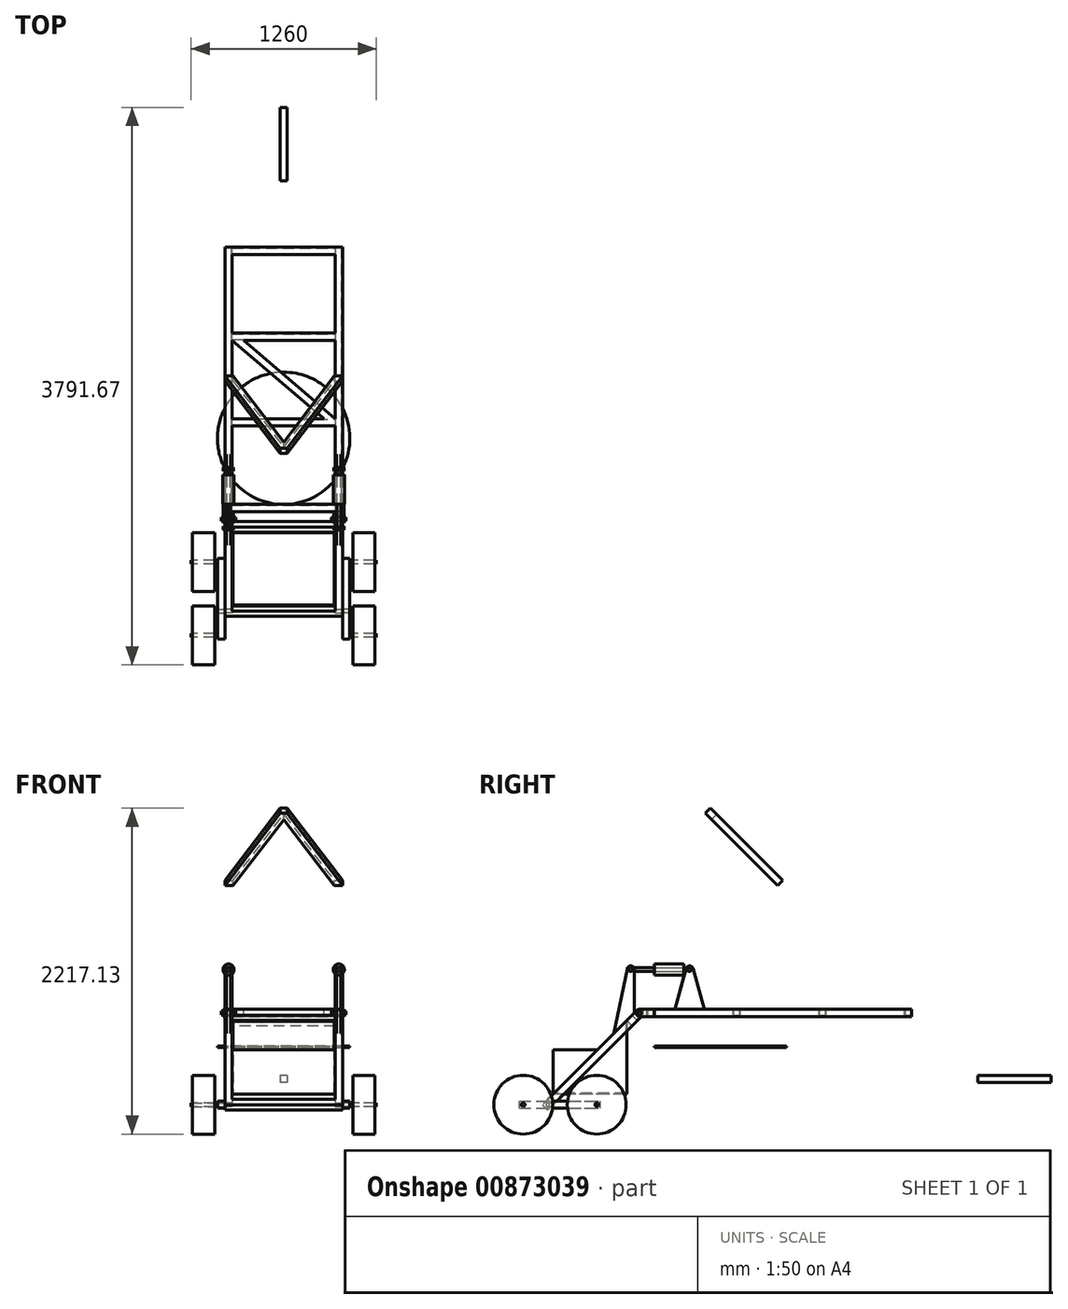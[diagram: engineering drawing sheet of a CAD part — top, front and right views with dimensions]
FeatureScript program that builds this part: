
annotation { "Feature Type Name" : "Feature", "Feature Type Description" : "" }
export const myFeature = defineFeature(function(context is Context, id is Id, definition is map)
    precondition{}
    {
        {
            assignVariable(context, id + "F0", {"name" : "TopLength", "anyValue" : 1800});
        }
        {
            assignVariable(context, id + "F1", {"name" : "PipeWidth", "anyValue" : 50});
        }
        {
            assignVariable(context, id + "F2", {"name" : "PipeThickness", "anyValue" : 5});
        }
        {
            var Q0;
            Q0=qCreatedBy(makeId("Front.planeOp"),FACE);
            var sketch = newSketch(context, id + "F3", { "sketchPlane" : qUnion([Q0])});
            skLineSegment(sketch, "E0.bottom", {"start": v(400, -25) * mm, "end": v(350, -25) * mm});
            skLineSegment(sketch, "E0.top", {"start": v(400, 25) * mm, "end": v(350, 25) * mm});
            skLineSegment(sketch, "E0.left", {"start": v(400, -25) * mm, "end": v(400, 25) * mm});
            skLineSegment(sketch, "E0.right", {"start": v(350, -25) * mm, "end": v(350, 25) * mm});
            skPoint(sketch, "E0.middle", {"position": v(375, 0) * mm});
            skSolve(sketch);
        }
        {
            var Q0;
            Q0=qSketchRegion(id+"F3",true);
            extrude(context, id + "F4", {"entities" : qUnion([Q0]), "endBound" : BoundingType.SYMMETRIC, "depth" : (getVariable(context, 'TopLength')) * mm, "offsetDistance" : 25 * mm});
        }
        {
            var Q0;
            Q0=makeQuery(id+"F4.opExtrude","CAP_FACE",FACE,{"disambiguationData":[OSD([sQuery(id+"F3.wireOp",EDGE,"E0.bottom"),sQuery(id+"F3.wireOp",EDGE,"E0.top"),sQuery(id+"F3.wireOp",EDGE,"E0.left"),sQuery(id+"F3.wireOp",EDGE,"E0.right")])],"isStart":false});
            var Q1;
            Q1=makeQuery(id+"F4.opExtrude","CAP_FACE",FACE,{"disambiguationData":[OSD([sQuery(id+"F3.wireOp",EDGE,"E0.bottom"),sQuery(id+"F3.wireOp",EDGE,"E0.top"),sQuery(id+"F3.wireOp",EDGE,"E0.left"),sQuery(id+"F3.wireOp",EDGE,"E0.right")])],"isStart":true});
            shell(context, id + "F5", {"entities" : qUnion([Q0, Q1]), "thickness" : (getVariable(context, 'PipeThickness')) * mm});
        }
        {
            var Q0;
            Q0=makeQuery(id+"F4.opExtrude","SWEPT_BODY",BODY,{"disambiguationData":[OSD([sQuery(id+"F3.wireOp",EDGE,"E0.bottom"),sQuery(id+"F3.wireOp",EDGE,"E0.top"),sQuery(id+"F3.wireOp",EDGE,"E0.left"),sQuery(id+"F3.wireOp",EDGE,"E0.right")])]});
            var Q1;
            Q1=qCreatedBy(makeId("Right.planeOp"),FACE);
            mirror(context, id + "F6", {"entities" : qUnion([Q0]), "mirrorPlane" : qUnion([Q1])});
        }
        {
            var Q0;
            Q0=makeQuery(id+"F4.opExtrude","SWEPT_FACE",FACE,{"disambiguationData":[OSD([sQuery(id+"F3.wireOp",EDGE,"E0.right")])]});
            var sketch = newSketch(context, id + "F7", { "sketchPlane" : qUnion([Q0])});
            skLineSegment(sketch, "E1.bottom", {"start": v(900, 25) * mm, "end": v(850, 25) * mm});
            skLineSegment(sketch, "E1.top", {"start": v(900, -25) * mm, "end": v(850, -25) * mm});
            skLineSegment(sketch, "E1.left", {"start": v(900, 25) * mm, "end": v(900, -25) * mm});
            skLineSegment(sketch, "E1.right", {"start": v(850, 25) * mm, "end": v(850, -25) * mm});
            skLineSegment(sketch, "E2.bottom", {"start": v(855, 20) * mm, "end": v(895, 20) * mm});
            skLineSegment(sketch, "E2.top", {"start": v(855, -20) * mm, "end": v(895, -20) * mm});
            skLineSegment(sketch, "E2.left", {"start": v(855, 20) * mm, "end": v(855, -20) * mm});
            skLineSegment(sketch, "E2.right", {"start": v(895, 20) * mm, "end": v(895, -20) * mm});
            skLineSegment(sketch, "E3.1.0.0", {"start": v(271.67, -20) * mm, "end": v(311.67, -20) * mm});
            skLineSegment(sketch, "E3.1.0.1", {"start": v(311.67, 20) * mm, "end": v(311.67, -20) * mm});
            skLineSegment(sketch, "E3.1.0.2", {"start": v(316.67, 25) * mm, "end": v(266.67, 25) * mm});
            skLineSegment(sketch, "E3.1.0.3", {"start": v(316.67, 25) * mm, "end": v(316.67, -25) * mm});
            skLineSegment(sketch, "E3.1.0.4", {"start": v(271.67, 20) * mm, "end": v(311.67, 20) * mm});
            skLineSegment(sketch, "E3.1.0.5", {"start": v(316.67, -25) * mm, "end": v(266.67, -25) * mm});
            skLineSegment(sketch, "E3.1.0.6", {"start": v(271.67, 20) * mm, "end": v(271.67, -20) * mm});
            skLineSegment(sketch, "E3.1.0.7", {"start": v(266.67, 25) * mm, "end": v(266.67, -25) * mm});
            skLineSegment(sketch, "E3.2.0.0", {"start": v(-311.67, -20) * mm, "end": v(-271.67, -20) * mm});
            skLineSegment(sketch, "E3.2.0.1", {"start": v(-271.67, 20) * mm, "end": v(-271.67, -20) * mm});
            skLineSegment(sketch, "E3.2.0.2", {"start": v(-266.67, 25) * mm, "end": v(-316.67, 25) * mm});
            skLineSegment(sketch, "E3.2.0.3", {"start": v(-266.67, 25) * mm, "end": v(-266.67, -25) * mm});
            skLineSegment(sketch, "E3.2.0.4", {"start": v(-311.67, 20) * mm, "end": v(-271.67, 20) * mm});
            skLineSegment(sketch, "E3.2.0.5", {"start": v(-266.67, -25) * mm, "end": v(-316.67, -25) * mm});
            skLineSegment(sketch, "E3.2.0.6", {"start": v(-311.67, 20) * mm, "end": v(-311.67, -20) * mm});
            skLineSegment(sketch, "E3.2.0.7", {"start": v(-316.67, 25) * mm, "end": v(-316.67, -25) * mm});
            skLineSegment(sketch, "E3.3.0.0", {"start": v(-895, -20) * mm, "end": v(-855, -20) * mm});
            skLineSegment(sketch, "E3.3.0.1", {"start": v(-855, 20) * mm, "end": v(-855, -20) * mm});
            skLineSegment(sketch, "E3.3.0.2", {"start": v(-850, 25) * mm, "end": v(-900, 25) * mm});
            skLineSegment(sketch, "E3.3.0.3", {"start": v(-850, 25) * mm, "end": v(-850, -25) * mm});
            skLineSegment(sketch, "E3.3.0.4", {"start": v(-895, 20) * mm, "end": v(-855, 20) * mm});
            skLineSegment(sketch, "E3.3.0.5", {"start": v(-850, -25) * mm, "end": v(-900, -25) * mm});
            skLineSegment(sketch, "E3.3.0.6", {"start": v(-895, 20) * mm, "end": v(-895, -20) * mm});
            skLineSegment(sketch, "E3.3.0.7", {"start": v(-900, 25) * mm, "end": v(-900, -25) * mm});
            skLineSegment(sketch, "E3.direction1", {"start": v(850, -25) * mm, "end": v(266.67, -25) * mm, "construction": true});
            skSolve(sketch);
        }
        {
            var Q0;
            Q0=qSketchRegion(id+"F7",true);
            extrude(context, id + "F8", {"entities" : qUnion([Q0]), "operationType" : NewBodyOperationType.ADD, "endBound" : BoundingType.UP_TO_NEXT, "depth" : 25 * mm, "offsetDistance" : 25 * mm});
        }
        {
            assignVariable(context, id + "F9", {"name" : "TopHeight", "anyValue" : 800});
        }
        {
            var Q0;
            {var subQ0=makeQuery(id+"F4.opExtrude","SWEPT_FACE",FACE,{"disambiguationData":[OSD([sQuery(id+"F3.wireOp",EDGE,"E0.bottom")])]});Q0=makeQuery(id+"F8.boolean.opBoolean","MERGE",FACE,{"derivedFrom":[subQ0,makeQuery(id+"F6.opPattern","COPY",FACE,{"derivedFrom":subQ0,"instanceName":"1"}),makeQuery(id+"F8.opExtrude","SWEPT_FACE",FACE,{"disambiguationData":[OSD([sQuery(id+"F7.wireOp",EDGE,"E1.top")])]}),makeQuery(id+"F8.opExtrude","SWEPT_FACE",FACE,{"disambiguationData":[OSD([sQuery(id+"F7.wireOp",EDGE,"E3.1.0.5")])]}),makeQuery(id+"F8.opExtrude","SWEPT_FACE",FACE,{"disambiguationData":[OSD([sQuery(id+"F7.wireOp",EDGE,"E3.2.0.5")])]}),makeQuery(id+"F8.opExtrude","SWEPT_FACE",FACE,{"disambiguationData":[OSD([sQuery(id+"F7.wireOp",EDGE,"E3.3.0.5")])]})]});}
            cPlane(context, id + "F10", {"entities" : qUnion([Q0]), "cplaneType" : CPlaneType.OFFSET, "offset" : (getVariable(context, 'TopHeight')) * mm, "width" : 150 * mm, "height" : 150 * mm});
        }
        {
            var Q0;
            Q0=makeQuery(id+"F6.opPattern","COPY",FACE,{"derivedFrom":makeQuery(id+"F4.opExtrude","SWEPT_FACE",FACE,{"disambiguationData":[OSD([sQuery(id+"F3.wireOp",EDGE,"E0.left")])]}),"instanceName":"1"});
            var sketch = newSketch(context, id + "F11", { "sketchPlane" : qUnion([Q0])});
            skLineSegment(sketch, "E4", {"start": v(967.68, 17.68) * mm, "end": v(1610.36, -625) * mm});
            skLineSegment(sketch, "E5", {"start": v(1610.36, -625) * mm, "end": v(1575, -660.36) * mm});
            skLineSegment(sketch, "E6", {"start": v(1575, -660.36) * mm, "end": v(932.32, -17.68) * mm});
            skCircle(sketch, "E7", {"center": v(1092.75, -625) * mm, "radius": 200 * mm, "construction": true});
            skCircle(sketch, "E8", {"center": v(1592.75, -625) * mm, "radius": 200 * mm, "construction": true});
            skCircle(sketch, "E9", {"center": v(1575, -625) * mm, "radius": 12.5 * mm});
            skLineSegment(sketch, "E10", {"start": v(1575, -625) * mm, "end": v(1615.74, -665.74) * mm, "construction": true});
            skCircle(sketch, "E11", {"center": v(950, 0) * mm, "radius": 12.5 * mm});
            skPoint(sketch, "E11.centerSnap0", {"position": v(900, 0) * mm});
            skLineSegment(sketch, "E12", {"start": v(950, 0) * mm, "end": v(1014.37, -64.37) * mm, "construction": true});
            skArc(sketch, "E13", {"start": v(967.68, 17.68) * mm, "mid": v(932.32, 17.68) * mm, "end": v(932.32, -17.68) * mm});
            skSolve(sketch);
        }
        {
            var Q0;
            Q0=qSketchRegion(id+"F11",true);
            extrude(context, id + "F12", {"entities" : qUnion([Q0]), "oppositeDirection" : true, "depth" : (getVariable(context, 'PipeWidth')) * mm, "offsetDistance" : 25 * mm});
        }
        {
            var Q0;
            Q0=makeQuery(id+"F12.opExtrude","SWEPT_BODY",BODY,{"disambiguationData":[OSD([sQuery(id+"F11.wireOp",EDGE,"E4"),sQuery(id+"F11.wireOp",EDGE,"E5"),sQuery(id+"F11.wireOp",EDGE,"E6"),sQuery(id+"F11.wireOp",EDGE,"p147dLJD-aIzN-PVzP-jr04-d3EFBxcOCl1r"),sQuery(id+"F11.wireOp",EDGE,"E9")])]});
            var Q1;
            Q1=qCreatedBy(makeId("Right.planeOp"),FACE);
            mirror(context, id + "F13", {"operationType" : NewBodyOperationType.ADD, "entities" : qUnion([Q0]), "mirrorPlane" : qUnion([Q1])});
        }
        {
            var Q0;
            Q0=makeQuery(id+"F12.opExtrude","CAP_FACE",FACE,{"disambiguationData":[OSD([sQuery(id+"F11.wireOp",EDGE,"E4"),sQuery(id+"F11.wireOp",EDGE,"E5"),sQuery(id+"F11.wireOp",EDGE,"E6"),sQuery(id+"F11.wireOp",EDGE,"E9"),sQuery(id+"F11.wireOp",EDGE,"E11"),sQuery(id+"F11.wireOp",EDGE,"E13")])],"isStart":false});
            var sketch = newSketch(context, id + "F14", { "sketchPlane" : qUnion([Q0])});
            skLineSegment(sketch, "E14", {"start": v(-1575, -660.36) * mm, "end": v(-1539.64, -625) * mm});
            skLineSegment(sketch, "E15", {"start": v(-1575, -589.64) * mm, "end": v(-1539.64, -625) * mm});
            skLineSegment(sketch, "E16", {"start": v(-1575, -589.64) * mm, "end": v(-1610.36, -625) * mm});
            skLineSegment(sketch, "E17", {"start": v(-1575, -660.36) * mm, "end": v(-1610.36, -625) * mm});
            skSolve(sketch);
        }
        {
            var Q0;
            Q0=qSketchRegion(id+"F14",true);
            var Q1;
            Q1=makeQuery(id+"F13.opPattern","COPY",FACE,{"derivedFrom":makeQuery(id+"F12.opExtrude","CAP_FACE",FACE,{"disambiguationData":[OSD([sQuery(id+"F11.wireOp",EDGE,"E4"),sQuery(id+"F11.wireOp",EDGE,"E5"),sQuery(id+"F11.wireOp",EDGE,"E6"),sQuery(id+"F11.wireOp",EDGE,"E9"),sQuery(id+"F11.wireOp",EDGE,"E11"),sQuery(id+"F11.wireOp",EDGE,"E13")])],"isStart":false}),"instanceName":"1"});
            extrude(context, id + "F15", {"entities" : qUnion([Q0]), "operationType" : NewBodyOperationType.ADD, "endBound" : BoundingType.UP_TO_SURFACE, "depth" : (50 + 15) * mm, "endBoundEntityFace" : qUnion([Q1]), "offsetDistance" : 25 * mm});
        }
        {
            var Q0;
            Q0=makeQuery(id+"F13.boolean.opBoolean","MERGE",FACE,{"derivedFrom":[makeQuery(id+"F6.opPattern","COPY",FACE,{"derivedFrom":makeQuery(id+"F4.opExtrude","SWEPT_FACE",FACE,{"disambiguationData":[OSD([sQuery(id+"F3.wireOp",EDGE,"E0.left")])]}),"instanceName":"1"}),makeQuery(id+"F12.opExtrude","CAP_FACE",FACE,{"disambiguationData":[OSD([sQuery(id+"F11.wireOp",EDGE,"E4"),sQuery(id+"F11.wireOp",EDGE,"E5"),sQuery(id+"F11.wireOp",EDGE,"E6"),sQuery(id+"F11.wireOp",EDGE,"p147dLJD-aIzN-PVzP-jr04-d3EFBxcOCl1r"),sQuery(id+"F11.wireOp",EDGE,"E9")])],"isStart":true})]});
            var sketch = newSketch(context, id + "F16", { "sketchPlane" : qUnion([Q0])});
            skCircle(sketch, "E18.0.0", {"center": v(1575, -625) * mm, "radius": 12.5 * mm});
            skLineSegment(sketch, "E19.bottom", {"start": v(1766.67, -650) * mm, "end": v(1216.67, -650) * mm});
            skLineSegment(sketch, "E19.top", {"start": v(1766.67, -600) * mm, "end": v(1216.67, -600) * mm});
            skLineSegment(sketch, "E19.left", {"start": v(1766.67, -650) * mm, "end": v(1766.67, -600) * mm});
            skLineSegment(sketch, "E19.right", {"start": v(1216.67, -650) * mm, "end": v(1216.67, -600) * mm});
            skPoint(sketch, "E19.middle", {"position": v(1491.67, -625) * mm});
            skCircle(sketch, "E20", {"center": v(1741.67, -625) * mm, "radius": 12.5 * mm});
            skCircle(sketch, "E21", {"center": v(1241.67, -625) * mm, "radius": 12.5 * mm});
            skSolve(sketch);
        }
        {
            var Q0;
            Q0=qSketchRegion(id+"F16",true);
            extrude(context, id + "F17", {"entities" : qUnion([Q0]), "depth" : (getVariable(context, 'PipeWidth')) * mm, "offsetDistance" : 25 * mm});
        }
        {
            var Q0;
            Q0=makeQuery(id+"F17.opExtrude","CAP_FACE",FACE,{"disambiguationData":[OSD([sQuery(id+"F16.wireOp",EDGE,"E18.0.0"),sQuery(id+"F16.wireOp",EDGE,"E19.bottom"),sQuery(id+"F16.wireOp",EDGE,"E19.top"),sQuery(id+"F16.wireOp",EDGE,"E19.left"),sQuery(id+"F16.wireOp",EDGE,"E19.right"),sQuery(id+"F16.wireOp",EDGE,"E20"),sQuery(id+"F16.wireOp",EDGE,"E21")])],"isStart":false});
            var sketch = newSketch(context, id + "F18", { "sketchPlane" : qUnion([Q0])});
            skCircle(sketch, "E22.0", {"center": v(1741.67, -625) * mm, "radius": 12.5 * mm});
            skCircle(sketch, "E23.0", {"center": v(1241.67, -625) * mm, "radius": 12.5 * mm});
            skSolve(sketch);
        }
        {
            var Q0;
            Q0=qSketchRegion(id+"F18",true);
            var Q1;
            Q1=makeQuery(id+"F17.opExtrude","CAP_FACE",FACE,{"disambiguationData":[OSD([sQuery(id+"F16.wireOp",EDGE,"E18.0.0"),sQuery(id+"F16.wireOp",EDGE,"E19.bottom"),sQuery(id+"F16.wireOp",EDGE,"E19.top"),sQuery(id+"F16.wireOp",EDGE,"E19.left"),sQuery(id+"F16.wireOp",EDGE,"E19.right"),sQuery(id+"F16.wireOp",EDGE,"E20"),sQuery(id+"F16.wireOp",EDGE,"E21")])],"isStart":true});
            extrude(context, id + "F19", {"entities" : qUnion([Q0]), "operationType" : NewBodyOperationType.ADD, "depth" : (20 + 150 + 10) * mm, "offsetDistance" : 25 * mm, "hasSecondDirection" : true, "secondDirectionBound" : SecondDirectionBoundingType.UP_TO_SURFACE, "secondDirectionOppositeDirection" : true, "secondDirectionDepth" : 25 * mm, "secondDirectionBoundEntityFace" : qUnion([Q1])});
        }
        {
            var Q0;
            Q0=makeQuery(id+"F19.opExtrude","CAP_FACE",FACE,{"disambiguationData":[OSD([sQuery(id+"F18.wireOp",EDGE,"E23.0")])],"isStart":false});
            cPlane(context, id + "F20", {"entities" : qUnion([Q0]), "cplaneType" : CPlaneType.OFFSET, "offset" : 10 * mm, "oppositeDirection" : true, "width" : 150 * mm, "height" : 150 * mm});
        }
        {
            var Q0;
            Q0=qCreatedBy(id+"F20.planeOp",FACE);
            var sketch = newSketch(context, id + "F21", { "sketchPlane" : qUnion([Q0])});
            skCircle(sketch, "E24.0", {"center": v(1241.67, -625) * mm, "radius": 12.5 * mm});
            skCircle(sketch, "E25.0.0", {"center": v(1741.67, -625) * mm, "radius": 12.5 * mm});
            skCircle(sketch, "E26", {"center": v(1241.67, -625) * mm, "radius": 200 * mm});
            skCircle(sketch, "E27", {"center": v(1741.67, -625) * mm, "radius": 200 * mm});
            skSolve(sketch);
        }
        {
            var Q0;
            Q0=qSketchRegion(id+"F21",true);
            extrude(context, id + "F22", {"entities" : qUnion([Q0]), "oppositeDirection" : true, "depth" : 150 * mm, "offsetDistance" : 25 * mm});
        }
        {
            var Q0;
            Q0=makeQuery(id+"F22.opExtrude","SWEPT_BODY",BODY,{"disambiguationData":[OSD([sQuery(id+"F21.wireOp",EDGE,"E24.0"),sQuery(id+"F21.wireOp",EDGE,"E26")])]});
            var Q1;
            Q1=makeQuery(id+"F22.opExtrude","SWEPT_BODY",BODY,{"disambiguationData":[OSD([sQuery(id+"F21.wireOp",EDGE,"E25.0.0"),sQuery(id+"F21.wireOp",EDGE,"E27")])]});
            var Q2;
            Q2=makeQuery(id+"F17.opExtrude","SWEPT_BODY",BODY,{"disambiguationData":[OSD([sQuery(id+"F16.wireOp",EDGE,"E18.0.0"),sQuery(id+"F16.wireOp",EDGE,"E19.bottom"),sQuery(id+"F16.wireOp",EDGE,"E19.top"),sQuery(id+"F16.wireOp",EDGE,"E19.left"),sQuery(id+"F16.wireOp",EDGE,"E19.right"),sQuery(id+"F16.wireOp",EDGE,"E20"),sQuery(id+"F16.wireOp",EDGE,"E21")])]});
            var Q3;
            Q3=qCreatedBy(makeId("Right.planeOp"),FACE);
            mirror(context, id + "F23", {"entities" : qUnion([Q0, Q1, Q2]), "mirrorPlane" : qUnion([Q3])});
        }
        {
            var Q0;
            Q0=qCreatedBy(makeId("Right.planeOp"),FACE);
            var sketch = newSketch(context, id + "F24", { "sketchPlane" : qUnion([Q0])});
            skLineSegment(sketch, "E28.bottom", {"start": v(1850, -425) * mm, "end": v(1350, -425) * mm});
            skLineSegment(sketch, "E28.top", {"start": v(1850, -475) * mm, "end": v(1350, -475) * mm});
            skLineSegment(sketch, "E28.left", {"start": v(1850, -425) * mm, "end": v(1850, -475) * mm});
            skLineSegment(sketch, "E28.right", {"start": v(1350, -425) * mm, "end": v(1350, -475) * mm});
            skLineSegment(sketch, "E29", {"start": v(1350, -425) * mm, "end": v(900, 25) * mm, "construction": true});
            skSolve(sketch);
        }
        {
            var Q0;
            Q0=qSketchRegion(id+"F24",true);
            extrude(context, id + "F25", {"entities" : qUnion([Q0]), "endBound" : BoundingType.SYMMETRIC, "depth" : (getVariable(context, 'PipeWidth')) * mm, "offsetDistance" : 25 * mm});
        }
        {
            var Q0;
            Q0=makeQuery(id+"F4.opExtrude","CAP_VERTEX",VERTEX,{"disambiguationData":[OSD([sQuery(id+"F3.wireOp",EDGE,"E0.top"),sQuery(id+"F3.wireOp",EDGE,"E0.left")])],"isStart":true});
            var Q1;
            Q1=makeQuery(id+"F6.opPattern","COPY",VERTEX,{"derivedFrom":makeQuery(id+"F4.opExtrude","CAP_VERTEX",VERTEX,{"disambiguationData":[OSD([sQuery(id+"F3.wireOp",EDGE,"E0.top"),sQuery(id+"F3.wireOp",EDGE,"E0.left")])],"isStart":true}),"instanceName":"1"});
            var Q2;
            Q2=makeQuery(id+"F25.opExtrude","CAP_VERTEX",VERTEX,{"disambiguationData":[OSD([sQuery(id+"F24.wireOp",EDGE,"E28.bottom"),sQuery(id+"F24.wireOp",EDGE,"E28.right")])],"isStart":true});
            cPlane(context, id + "F26", {"entities" : qUnion([Q0, Q1, Q2]), "cplaneType" : CPlaneType.THREE_POINT, "offset" : 25 * mm, "width" : 150 * mm, "height" : 150 * mm});
        }
        {
            var Q0;
            Q0=qCreatedBy(id+"F26.planeOp",FACE);
            var sketch = newSketch(context, id + "F27", { "sketchPlane" : qUnion([Q0])});
            skLineSegment(sketch, "E30", {"start": v(400, 618.72) * mm, "end": v(25, 1314.7) * mm});
            skLineSegment(sketch, "E31", {"start": v(25, 1314.7) * mm, "end": v(-25, 1314.7) * mm});
            skLineSegment(sketch, "E32", {"start": v(-25, 1314.7) * mm, "end": v(-400, 618.72) * mm});
            skLineSegment(sketch, "E33", {"start": v(400, 618.72) * mm, "end": v(343.2, 618.72) * mm});
            skLineSegment(sketch, "E34", {"start": v(343.2, 618.72) * mm, "end": v(0, 1255.7) * mm});
            skLineSegment(sketch, "E35", {"start": v(0, 1255.7) * mm, "end": v(-343.2, 618.72) * mm});
            skLineSegment(sketch, "E36", {"start": v(-343.2, 618.72) * mm, "end": v(-400, 618.72) * mm});
            skSolve(sketch);
        }
        {
            var Q0;
            Q0=qSketchRegion(id+"F27",true);
            extrude(context, id + "F28", {"entities" : qUnion([Q0]), "operationType" : NewBodyOperationType.ADD, "oppositeDirection" : true, "depth" : 50 * mm, "offsetDistance" : 25 * mm});
        }
        {
            var Q0;
            Q0=makeQuery(id+"F6.opPattern","COPY",FACE,{"derivedFrom":makeQuery(id+"F4.opExtrude","SWEPT_FACE",FACE,{"disambiguationData":[OSD([sQuery(id+"F3.wireOp",EDGE,"E0.left")])]}),"instanceName":"1"});
            var sketch = newSketch(context, id + "F29", { "sketchPlane" : qUnion([Q0])});
            skLineSegment(sketch, "E37", {"start": v(850, 25) * mm, "end": v(850, -25) * mm});
            skLineSegment(sketch, "E38", {"start": v(850, -25) * mm, "end": v(950, -25) * mm});
            skLineSegment(sketch, "E39", {"start": v(850, 25) * mm, "end": v(950, 25) * mm});
            skCircle(sketch, "E40.0", {"center": v(950, 0) * mm, "radius": 12.5 * mm});
            skArc(sketch, "E41", {"start": v(950, 25) * mm, "mid": v(975, 0) * mm, "end": v(950, -25) * mm});
            skSolve(sketch);
        }
        {
            var Q0;
            Q0 = qSketchRegion(id + "F29", true);
            extrude(context, id + "F30", {"entities" : qUnion([Q0]), "depth" : 10 * mm, "offsetDistance" : 25 * mm});
        }
        {
            var Q0;
            Q0=makeQuery(id+"F12.opExtrude","CAP_FACE",FACE,{"disambiguationData":[OSD([sQuery(id+"F11.wireOp",EDGE,"E4"),sQuery(id+"F11.wireOp",EDGE,"E5"),sQuery(id+"F11.wireOp",EDGE,"E6"),sQuery(id+"F11.wireOp",EDGE,"E9"),sQuery(id+"F11.wireOp",EDGE,"E11"),sQuery(id+"F11.wireOp",EDGE,"E13")])],"isStart":false});
            var sketch = newSketch(context, id + "F31", { "sketchPlane" : qUnion([Q0])});
            skCircle(sketch, "E42.0", {"center": v(-950, 0) * mm, "radius": 12.5 * mm});
            skLineSegment(sketch, "E43", {"start": v(-950, -25) * mm, "end": v(-900, -25) * mm});
            skLineSegment(sketch, "E44", {"start": v(-900, -25) * mm, "end": v(-900, 25) * mm});
            skLineSegment(sketch, "E45", {"start": v(-900, 25) * mm, "end": v(-950, 25) * mm});
            skArc(sketch, "E46", {"start": v(-950, 25) * mm, "mid": v(-975, 0) * mm, "end": v(-950, -25) * mm});
            skSolve(sketch);
        }
        {
            var Q0;
            Q0 = qSketchRegion(id + "F31", true);
            extrude(context, id + "F32", {"entities" : qUnion([Q0]), "depth" : 10 * mm, "offsetDistance" : 25 * mm});
        }
        {
            var Q0;
            Q0=makeQuery(id+"F30.opExtrude","CAP_FACE",FACE,{"disambiguationData":[OSD([sQuery(id+"F29.wireOp",EDGE,"E37"),sQuery(id+"F29.wireOp",EDGE,"E38"),sQuery(id+"F29.wireOp",EDGE,"E39"),sQuery(id+"F29.wireOp",EDGE,"E40.0"),sQuery(id+"F29.wireOp",EDGE,"E41")])],"isStart":false});
            var sketch = newSketch(context, id + "F33", { "sketchPlane" : qUnion([Q0])});
            skCircle(sketch, "E47.0", {"center": v(950, 0) * mm, "radius": 12.5 * mm});
            skSolve(sketch);
        }
        {
            var Q0;
            Q0 = qSketchRegion(id + "F33", true);
            extrude(context, id + "F34", {"entities" : qUnion([Q0]), "depth" : 15 * mm, "offsetDistance" : 25 * mm, "hasSecondDirection" : true, "secondDirectionOppositeDirection" : true, "secondDirectionDepth" : (2 * 10 + 50 + 15) * mm});
        }
        {
            var Q0;
            Q0=makeQuery(id+"F34.opExtrude","SWEPT_BODY",BODY,{"disambiguationData":[OSD([sQuery(id+"F33.wireOp",EDGE,"E47.0")])]});
            var Q1;
            Q1=makeQuery(id+"F30.opExtrude","SWEPT_BODY",BODY,{"disambiguationData":[OSD([sQuery(id+"F29.wireOp",EDGE,"E37"),sQuery(id+"F29.wireOp",EDGE,"E38"),sQuery(id+"F29.wireOp",EDGE,"E39"),sQuery(id+"F29.wireOp",EDGE,"E40.0"),sQuery(id+"F29.wireOp",EDGE,"E41")])]});
            var Q2;
            Q2=makeQuery(id+"F32.opExtrude","SWEPT_BODY",BODY,{"disambiguationData":[OSD([sQuery(id+"F31.wireOp",EDGE,"E42.0"),sQuery(id+"F31.wireOp",EDGE,"E43"),sQuery(id+"F31.wireOp",EDGE,"E44"),sQuery(id+"F31.wireOp",EDGE,"E45"),sQuery(id+"F31.wireOp",EDGE,"E46")])]});
            var Q3;
            Q3=qCreatedBy(makeId("Right.planeOp"),FACE);
            mirror(context, id + "F35", {"entities" : qUnion([Q0, Q1, Q2]), "mirrorPlane" : qUnion([Q3])});
        }
        {
            var Q0;
            Q0=makeQuery(id+"F12.opExtrude","CAP_FACE",FACE,{"disambiguationData":[OSD([sQuery(id+"F11.wireOp",EDGE,"E4"),sQuery(id+"F11.wireOp",EDGE,"E5"),sQuery(id+"F11.wireOp",EDGE,"E6"),sQuery(id+"F11.wireOp",EDGE,"E9"),sQuery(id+"F11.wireOp",EDGE,"E11"),sQuery(id+"F11.wireOp",EDGE,"E13")])],"isStart":false});
            var sketch = newSketch(context, id + "F36", { "sketchPlane" : qUnion([Q0])});
            skLineSegment(sketch, "E48", {"start": v(-1003.03, -17.68) * mm, "end": v(-1038.39, -53.03) * mm});
            skLineSegment(sketch, "E49", {"start": v(-1038.39, -53.03) * mm, "end": v(-1003.03, -88.39) * mm});
            skLineSegment(sketch, "E50", {"start": v(-1003.03, -88.39) * mm, "end": v(-967.68, -53.03) * mm});
            skLineSegment(sketch, "E51", {"start": v(-967.68, -53.03) * mm, "end": v(-1003.03, -17.68) * mm});
            skCircle(sketch, "E52.0", {"center": v(-950, 0) * mm, "radius": 12.5 * mm, "construction": true});
            skSolve(sketch);
        }
        {
            var Q0;
            Q0 = qSketchRegion(id + "F36", true);
            extrude(context, id + "F37", {"entities" : qUnion([Q0]), "endBound" : BoundingType.UP_TO_NEXT, "depth" : 25 * mm, "offsetDistance" : 25 * mm});
        }
        {
            var Q0;
            {var subQ0=makeQuery(id+"F4.opExtrude","SWEPT_FACE",FACE,{"disambiguationData":[OSD([sQuery(id+"F3.wireOp",EDGE,"E0.top")])]});Q0=makeQuery(id+"F8.boolean.opBoolean","MERGE",FACE,{"derivedFrom":[subQ0,makeQuery(id+"F6.opPattern","COPY",FACE,{"derivedFrom":subQ0,"instanceName":"1"}),makeQuery(id+"F8.opExtrude","SWEPT_FACE",FACE,{"disambiguationData":[OSD([sQuery(id+"F7.wireOp",EDGE,"E1.bottom")])]}),makeQuery(id+"F8.opExtrude","SWEPT_FACE",FACE,{"disambiguationData":[OSD([sQuery(id+"F7.wireOp",EDGE,"E3.1.0.2")])]}),makeQuery(id+"F8.opExtrude","SWEPT_FACE",FACE,{"disambiguationData":[OSD([sQuery(id+"F7.wireOp",EDGE,"E3.2.0.2")])]}),makeQuery(id+"F8.opExtrude","SWEPT_FACE",FACE,{"disambiguationData":[OSD([sQuery(id+"F7.wireOp",EDGE,"E3.3.0.2")])]})]});}
            var sketch = newSketch(context, id + "F38", { "sketchPlane" : qUnion([Q0])});
            skLineSegment(sketch, "E53", {"start": v(350, -266.67) * mm, "end": v(-273.1, 266.67) * mm});
            skLineSegment(sketch, "E54", {"start": v(-273.1, 266.67) * mm, "end": v(-350, 266.67) * mm});
            skLineSegment(sketch, "E55", {"start": v(-350, 266.67) * mm, "end": v(273.1, -266.67) * mm});
            skLineSegment(sketch, "E56", {"start": v(273.1, -266.67) * mm, "end": v(350, -266.67) * mm});
            skSolve(sketch);
        }
        {
            var Q0;
            Q0 = qSketchRegion(id + "F38", true);
            extrude(context, id + "F39", {"entities" : qUnion([Q0]), "operationType" : NewBodyOperationType.ADD, "oppositeDirection" : true, "depth" : (getVariable(context, 'PipeWidth')) * mm, "offsetDistance" : 25 * mm});
        }
        {
            var Q0;
            Q0=makeQuery(id+"F12.opExtrude","CAP_FACE",FACE,{"disambiguationData":[OSD([sQuery(id+"F11.wireOp",EDGE,"E4"),sQuery(id+"F11.wireOp",EDGE,"E5"),sQuery(id+"F11.wireOp",EDGE,"E6"),sQuery(id+"F11.wireOp",EDGE,"E9"),sQuery(id+"F11.wireOp",EDGE,"E11"),sQuery(id+"F11.wireOp",EDGE,"E13")])],"isStart":true});
            var sketch = newSketch(context, id + "F40", { "sketchPlane" : qUnion([Q0])});
            skLineSegment(sketch, "E57", {"start": v(985.36, 0) * mm, "end": v(1126.78, -141.42) * mm});
            skLineSegment(sketch, "E58", {"start": v(1126.78, -141.42) * mm, "end": v(1034.83, 298.98) * mm});
            skLineSegment(sketch, "E59", {"start": v(985.36, 0) * mm, "end": v(985.36, 293.87) * mm});
            skArc(sketch, "E60", {"start": v(1034.83, 298.98) * mm, "mid": v(1007.79, 318.73) * mm, "end": v(985.36, 293.87) * mm});
            skCircle(sketch, "E61", {"center": v(1010.36, 293.87) * mm, "radius": 12.5 * mm});
            skCircle(sketch, "E62.0.0", {"center": v(950, 0) * mm, "radius": 12.5 * mm, "construction": true});
            skCircle(sketch, "E63", {"center": v(610.36, 293.87) * mm, "radius": 12.5 * mm});
            skLineSegment(sketch, "E64", {"start": v(586.25, 300.5) * mm, "end": v(510.36, 25) * mm});
            skLineSegment(sketch, "E65", {"start": v(510.36, 25) * mm, "end": v(710.36, 25) * mm});
            skLineSegment(sketch, "E66", {"start": v(710.36, 25) * mm, "end": v(634.46, 300.5) * mm});
            skArc(sketch, "E67", {"start": v(634.46, 300.5) * mm, "mid": v(610.36, 318.87) * mm, "end": v(586.25, 300.5) * mm});
            skLineSegment(sketch, "E68", {"start": v(610.36, 293.87) * mm, "end": v(610.36, 105.07) * mm, "construction": true});
            skSolve(sketch);
        }
        {
            var Q0;
            Q0 = qSketchRegion(id + "F40", true);
            extrude(context, id + "F41", {"entities" : qUnion([Q0]), "oppositeDirection" : true, "depth" : 10 * mm, "offsetDistance" : 25 * mm});
        }
        {
            var Q0;
            Q0=makeQuery(id+"F6.opPattern","COPY",FACE,{"derivedFrom":makeQuery(id+"F4.opExtrude","SWEPT_FACE",FACE,{"disambiguationData":[OSD([sQuery(id+"F3.wireOp",EDGE,"E0.left")])]}),"instanceName":"1"});
            var Q1;
            Q1=makeQuery(id+"F8.boolean.opBoolean","SPLIT",FACE,{"disambiguationData":[TD([makeQuery(id+"F8.opExtrude","SWEPT_FACE",FACE,{"disambiguationData":[OSD([sQuery(id+"F7.wireOp",EDGE,"E1.right")])]})])],"derivedFrom":makeQuery(id+"F6.opPattern","COPY",FACE,{"derivedFrom":makeQuery(id+"F4.opExtrude","SWEPT_FACE",FACE,{"disambiguationData":[OSD([sQuery(id+"F3.wireOp",EDGE,"E0.right")])]}),"instanceName":"1"})});
            cPlane(context, id + "F42", {"entities" : qUnion([Q0, Q1]), "cplaneType" : CPlaneType.MID_PLANE, "offset" : 25 * mm, "width" : 150 * mm, "height" : 150 * mm});
        }
        {
            var Q0;
            Q0=makeQuery(id+"F41.opExtrude","SWEPT_BODY",BODY,{"disambiguationData":[OSD([sQuery(id+"F40.wireOp",EDGE,"E57"),sQuery(id+"F40.wireOp",EDGE,"E58"),sQuery(id+"F40.wireOp",EDGE,"E59"),sQuery(id+"F40.wireOp",EDGE,"E60"),sQuery(id+"F40.wireOp",EDGE,"E61")])]});
            var Q1;
            Q1=makeQuery(id+"F41.opExtrude","SWEPT_BODY",BODY,{"disambiguationData":[OSD([sQuery(id+"F40.wireOp",EDGE,"E63"),sQuery(id+"F40.wireOp",EDGE,"E64"),sQuery(id+"F40.wireOp",EDGE,"E65"),sQuery(id+"F40.wireOp",EDGE,"E66"),sQuery(id+"F40.wireOp",EDGE,"E67")])]});
            var Q2;
            Q2=qCreatedBy(id+"F42.planeOp",FACE);
            mirror(context, id + "F43", {"entities" : qUnion([Q0, Q1]), "mirrorPlane" : qUnion([Q2])});
        }
        {
            var Q0;
            Q0=makeQuery(id+"F41.opExtrude","CAP_FACE",FACE,{"disambiguationData":[OSD([sQuery(id+"F40.wireOp",EDGE,"E63"),sQuery(id+"F40.wireOp",EDGE,"E64"),sQuery(id+"F40.wireOp",EDGE,"E65"),sQuery(id+"F40.wireOp",EDGE,"E66"),sQuery(id+"F40.wireOp",EDGE,"E67")])],"isStart":true});
            var sketch = newSketch(context, id + "F44", { "sketchPlane" : qUnion([Q0])});
            skCircle(sketch, "E69.0", {"center": v(610.36, 293.87) * mm, "radius": 12.5 * mm});
            skCircle(sketch, "E70.0", {"center": v(1010.36, 293.87) * mm, "radius": 12.5 * mm});
            skSolve(sketch);
        }
        {
            var Q0;
            Q0 = qSketchRegion(id + "F44", true);
            extrude(context, id + "F45", {"entities" : qUnion([Q0]), "depth" : 10 * mm, "offsetDistance" : 25 * mm, "hasSecondDirection" : true, "secondDirectionOppositeDirection" : true, "secondDirectionDepth" : 60 * mm});
        }
        {
            var Q0;
            Q0=makeQuery(id+"F8.opExtrude","SWEPT_FACE",FACE,{"disambiguationData":[OSD([sQuery(id+"F7.wireOp",EDGE,"E1.right")])]});
            var sketch = newSketch(context, id + "F46", { "sketchPlane" : qUnion([Q0])});
            skCircle(sketch, "E71", {"center": v(375, 293.87) * mm, "radius": 38.1 * mm});
            skLineSegment(sketch, "E72.0", {"start": v(410, 306.37) * mm, "end": v(410, 281.37) * mm, "construction": true});
            skLineSegment(sketch, "E73", {"start": v(375, 293.87) * mm, "end": v(410, 293.87) * mm, "construction": true});
            skLineSegment(sketch, "E74", {"start": v(375, 293.87) * mm, "end": v(375, 322.9) * mm, "construction": true});
            skSolve(sketch);
        }
        {
            var Q0;
            Q0 = qSketchRegion(id + "F46", true);
            extrude(context, id + "F47", {"entities" : qUnion([Q0]), "depth" : 200 * mm, "offsetDistance" : 25 * mm});
        }
        {
            var Q0;
            Q0=makeQuery(id+"F47.opExtrude","CAP_FACE",FACE,{"disambiguationData":[OSD([sQuery(id+"F46.wireOp",EDGE,"E71")])],"isStart":true});
            var sketch = newSketch(context, id + "F48", { "sketchPlane" : qUnion([Q0])});
            skCircle(sketch, "E75", {"center": v(-375, 293.87) * mm, "radius": 12.5 * mm});
            skSolve(sketch);
        }
        {
            var Q0;
            Q0 = qSketchRegion(id + "F48", true);
            var Q1;
            Q1=makeQuery(id+"F45.opExtrude","SWEPT_BODY",BODY,{"disambiguationData":[OSD([sQuery(id+"F44.wireOp",EDGE,"E69.0")])]});
            extrude(context, id + "F49", {"entities" : qUnion([Q0]), "endBound" : BoundingType.UP_TO_NEXT, "depth" : 25 * mm, "offsetDistance" : 25 * mm, "hasSecondDirection" : true, "secondDirectionBound" : SecondDirectionBoundingType.UP_TO_BODY, "secondDirectionOppositeDirection" : true, "secondDirectionDepth" : 25 * mm, "secondDirectionBoundEntityBody" : qUnion([Q1])});
        }
        {
            var Q0;
            Q0=makeQuery(id+"F45.opExtrude","SWEPT_BODY",BODY,{"disambiguationData":[OSD([sQuery(id+"F44.wireOp",EDGE,"E69.0")])]});
            var Q1;
            Q1=makeQuery(id+"F45.opExtrude","SWEPT_BODY",BODY,{"disambiguationData":[OSD([sQuery(id+"F44.wireOp",EDGE,"E70.0")])]});
            var Q2;
            Q2=makeQuery(id+"F41.opExtrude","SWEPT_BODY",BODY,{"disambiguationData":[OSD([sQuery(id+"F40.wireOp",EDGE,"E63"),sQuery(id+"F40.wireOp",EDGE,"E64"),sQuery(id+"F40.wireOp",EDGE,"E65"),sQuery(id+"F40.wireOp",EDGE,"E66"),sQuery(id+"F40.wireOp",EDGE,"E67")])]});
            var Q3;
            Q3=makeQuery(id+"F41.opExtrude","SWEPT_BODY",BODY,{"disambiguationData":[OSD([sQuery(id+"F40.wireOp",EDGE,"E57"),sQuery(id+"F40.wireOp",EDGE,"E58"),sQuery(id+"F40.wireOp",EDGE,"E59"),sQuery(id+"F40.wireOp",EDGE,"E60"),sQuery(id+"F40.wireOp",EDGE,"E61")])]});
            var Q4;
            Q4=makeQuery(id+"F47.opExtrude","SWEPT_BODY",BODY,{"disambiguationData":[OSD([sQuery(id+"F46.wireOp",EDGE,"E71")])]});
            var Q5;
            Q5=makeQuery(id+"F49.opExtrude","SWEPT_BODY",BODY,{"disambiguationData":[OSD([sQuery(id+"F48.wireOp",EDGE,"E75")])]});
            var Q6;
            Q6=makeQuery(id+"F43.opPattern","COPY",BODY,{"derivedFrom":makeQuery(id+"F41.opExtrude","SWEPT_BODY",BODY,{"disambiguationData":[OSD([sQuery(id+"F40.wireOp",EDGE,"E63"),sQuery(id+"F40.wireOp",EDGE,"E64"),sQuery(id+"F40.wireOp",EDGE,"E65"),sQuery(id+"F40.wireOp",EDGE,"E66"),sQuery(id+"F40.wireOp",EDGE,"E67")])]}),"instanceName":"1"});
            var Q7;
            Q7=makeQuery(id+"F43.opPattern","COPY",BODY,{"derivedFrom":makeQuery(id+"F41.opExtrude","SWEPT_BODY",BODY,{"disambiguationData":[OSD([sQuery(id+"F40.wireOp",EDGE,"E57"),sQuery(id+"F40.wireOp",EDGE,"E58"),sQuery(id+"F40.wireOp",EDGE,"E59"),sQuery(id+"F40.wireOp",EDGE,"E60"),sQuery(id+"F40.wireOp",EDGE,"E61")])]}),"instanceName":"1"});
            var Q8;
            Q8=qCreatedBy(makeId("Right.planeOp"),FACE);
            mirror(context, id + "F50", {"entities" : qUnion([Q0, Q1, Q2, Q3, Q4, Q5, Q6, Q7]), "mirrorPlane" : qUnion([Q8])});
        }
        {
            var Q0;
            Q0=makeQuery(id+"F13.opPattern","COPY",FACE,{"derivedFrom":makeQuery(id+"F12.opExtrude","CAP_FACE",FACE,{"disambiguationData":[OSD([sQuery(id+"F11.wireOp",EDGE,"E4"),sQuery(id+"F11.wireOp",EDGE,"E5"),sQuery(id+"F11.wireOp",EDGE,"E6"),sQuery(id+"F11.wireOp",EDGE,"E9"),sQuery(id+"F11.wireOp",EDGE,"E11"),sQuery(id+"F11.wireOp",EDGE,"E13")])],"isStart":false}),"instanceName":"1"});
            var sketch = newSketch(context, id + "F51", { "sketchPlane" : qUnion([Q0])});
            skLineSegment(sketch, "E76", {"start": v(1038.39, -53.03) * mm, "end": v(1038.39, -553.03) * mm});
            skLineSegment(sketch, "E77", {"start": v(1038.39, -553.03) * mm, "end": v(1538.39, -553.03) * mm});
            skLineSegment(sketch, "E78", {"start": v(1538.39, -553.03) * mm, "end": v(1538.39, -253.03) * mm});
            skLineSegment(sketch, "E79", {"start": v(1538.39, -253.03) * mm, "end": v(1238.39, -253.03) * mm});
            skLineSegment(sketch, "E80", {"start": v(1238.39, -253.03) * mm, "end": v(1038.39, -53.03) * mm});
            skSolve(sketch);
        }
        {
            var Q0;
            Q0 = qSketchRegion(id + "F51", true);
            var Q1;
            Q1=makeQuery(id+"F12.opExtrude","CAP_FACE",FACE,{"disambiguationData":[OSD([sQuery(id+"F11.wireOp",EDGE,"E4"),sQuery(id+"F11.wireOp",EDGE,"E5"),sQuery(id+"F11.wireOp",EDGE,"E6"),sQuery(id+"F11.wireOp",EDGE,"E9"),sQuery(id+"F11.wireOp",EDGE,"E11"),sQuery(id+"F11.wireOp",EDGE,"E13")])],"isStart":false});
            extrude(context, id + "F52", {"entities" : qUnion([Q0]), "endBound" : BoundingType.UP_TO_SURFACE, "depth" : 25 * mm, "endBoundEntityFace" : qUnion([Q1]), "offsetDistance" : 25 * mm});
        }
        {
            var Q0;
            Q0=makeQuery(id+"F52.opExtrude","SWEPT_FACE",FACE,{"disambiguationData":[OSD([sQuery(id+"F51.wireOp",EDGE,"E80")])]});
            var Q1;
            Q1=makeQuery(id+"F52.opExtrude","SWEPT_FACE",FACE,{"disambiguationData":[OSD([sQuery(id+"F51.wireOp",EDGE,"E79")])]});
            shell(context, id + "F53", {"entities" : qUnion([Q0, Q1]), "thickness" : 5 * mm});
        }
        {
            var Q0;
            {var subQ0=makeQuery(id+"F4.opExtrude","SWEPT_FACE",FACE,{"disambiguationData":[OSD([sQuery(id+"F3.wireOp",EDGE,"E0.bottom")])]});Q0=makeQuery(id+"F39.boolean.opBoolean","MERGE",FACE,{"derivedFrom":[makeQuery(id+"F8.boolean.opBoolean","MERGE",FACE,{"derivedFrom":[subQ0,makeQuery(id+"F6.opPattern","COPY",FACE,{"derivedFrom":subQ0,"instanceName":"1"}),makeQuery(id+"F8.opExtrude","SWEPT_FACE",FACE,{"disambiguationData":[OSD([sQuery(id+"F7.wireOp",EDGE,"E1.top")])]}),makeQuery(id+"F8.opExtrude","SWEPT_FACE",FACE,{"disambiguationData":[OSD([sQuery(id+"F7.wireOp",EDGE,"E3.1.0.5")])]}),makeQuery(id+"F8.opExtrude","SWEPT_FACE",FACE,{"disambiguationData":[OSD([sQuery(id+"F7.wireOp",EDGE,"E3.2.0.5")])]}),makeQuery(id+"F8.opExtrude","SWEPT_FACE",FACE,{"disambiguationData":[OSD([sQuery(id+"F7.wireOp",EDGE,"E3.3.0.5")])]})]}),makeQuery(id+"F39.opExtrude","CAP_FACE",FACE,{"disambiguationData":[OSD([sQuery(id+"F38.wireOp",EDGE,"E53"),sQuery(id+"F38.wireOp",EDGE,"E54"),sQuery(id+"F38.wireOp",EDGE,"E55"),sQuery(id+"F38.wireOp",EDGE,"E56")])],"isStart":false})]});}
            cPlane(context, id + "F54", {"entities" : qUnion([Q0]), "cplaneType" : CPlaneType.OFFSET, "offset" : 200 * mm, "width" : 150 * mm, "height" : 150 * mm});
        }
        {
            var Q0;
            Q0=qCreatedBy(id+"F54.planeOp",FACE);
            var sketch = newSketch(context, id + "F55", { "sketchPlane" : qUnion([Q0])});
            skCircle(sketch, "E81", {"center": v(0, 400) * mm, "radius": 450 * mm});
            skSolve(sketch);
        }
        {
            var Q0;
            Q0 = qSketchRegion(id + "F55", true);
            extrude(context, id + "F56", {"entities" : qUnion([Q0]), "depth" : 10 * mm, "offsetDistance" : 25 * mm});
        }
    });
